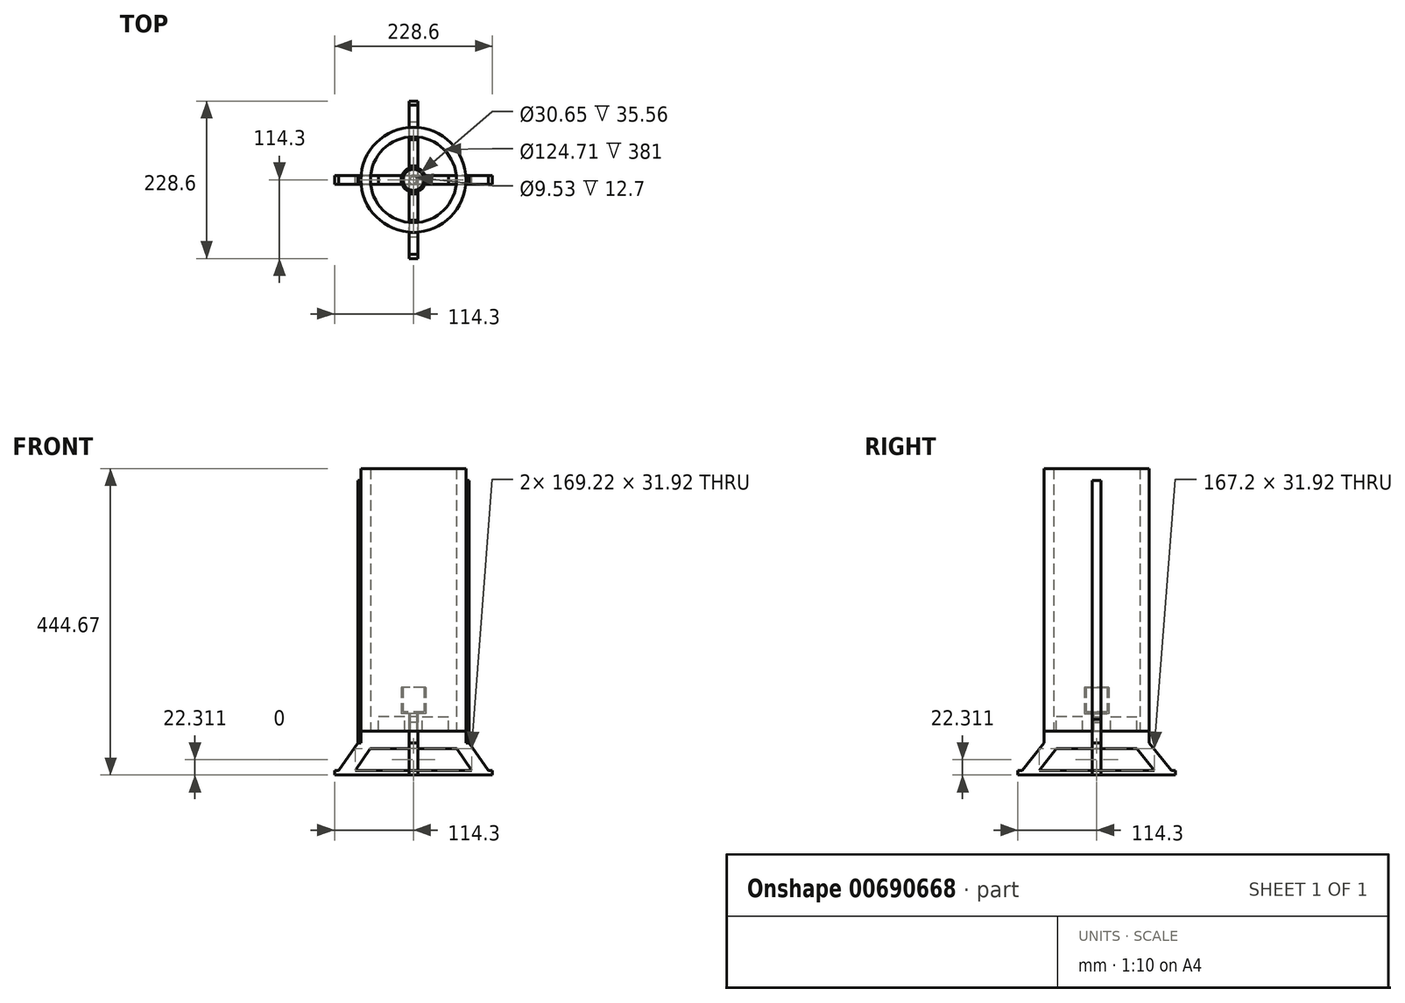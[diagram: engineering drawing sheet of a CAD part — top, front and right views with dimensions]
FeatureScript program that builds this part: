
annotation { "Feature Type Name" : "Feature", "Feature Type Description" : "" }
export const myFeature = defineFeature(function(context is Context, id is Id, definition is map)
    precondition{}
    {
        {
            var Q0;
            Q0=qCreatedBy(makeId("Top.planeOp"),FACE);
            var sketch = newSketch(context, id + "F0", { "sketchPlane" : qUnion([Q0])});
            skCircle(sketch, "E0", {"center": v(0, 0) * mm, "radius": 76.2 * mm});
            skCircle(sketch, "E1.0", {"center": v(0, 0) * mm, "radius": 62.36 * mm});
            skSolve(sketch);
        }
        {
            var Q0;
            Q0=qSketchRegion(id+"F0",true);
            extrude(context, id + "F1", {"entities" : qUnion([Q0]), "depth" : 381 * mm, "offsetDistance" : 25.4 * mm});
        }
        {
            var Q0;
            Q0=qCreatedBy(makeId("Front.planeOp"),FACE);
            var sketch = newSketch(context, id + "F2", { "sketchPlane" : qUnion([Q0])});
            skLineSegment(sketch, "E2", {"start": v(0, 0) * mm, "end": v(76.2, 0) * mm});
            skLineSegment(sketch, "E3", {"start": v(84.61, -57.32) * mm, "end": v(62.97, -25.4) * mm});
            skLineSegment(sketch, "E4", {"start": v(62.97, -25.4) * mm, "end": v(0, -25.4) * mm});
            skLineSegment(sketch, "E5", {"start": v(76.2, 0) * mm, "end": v(76.2, -16.95) * mm});
            skLineSegment(sketch, "E6", {"start": v(76.2, -16.95) * mm, "end": v(80.84, -16.95) * mm});
            skLineSegment(sketch, "E7", {"start": v(80.84, -16.95) * mm, "end": v(108.66, -57.32) * mm});
            skLineSegment(sketch, "E8", {"start": v(0, 0) * mm, "end": v(0, -25.4) * mm});
            skLineSegment(sketch, "E9", {"start": v(108.66, -57.32) * mm, "end": v(84.61, -57.32) * mm});
            skLineSegment(sketch, "E10.bottom", {"start": v(0, -57.32) * mm, "end": v(0, -57.32) * mm});
            skLineSegment(sketch, "E10.left", {"start": v(0, -57.32) * mm, "end": v(0, -63.67) * mm});
            skLineSegment(sketch, "E10.right", {"start": v(0, -57.32) * mm, "end": v(0, -63.67) * mm});
            skLineSegment(sketch, "E11.bottom", {"start": v(0, -57.32) * mm, "end": v(114.3, -57.32) * mm});
            skLineSegment(sketch, "E11.top", {"start": v(0, -63.67) * mm, "end": v(114.3, -63.67) * mm});
            skLineSegment(sketch, "E11.right", {"start": v(114.3, -57.32) * mm, "end": v(114.3, -63.67) * mm});
            skLineSegment(sketch, "E12.MirrorCS", {"start": v(-76.2, -16.95) * mm, "end": v(-80.84, -16.95) * mm});
            skLineSegment(sketch, "E13.MirrorCS", {"start": v(-76.2, 0) * mm, "end": v(-76.2, -16.95) * mm});
            skLineSegment(sketch, "E14.MirrorCS", {"start": v(-108.66, -57.32) * mm, "end": v(-84.61, -57.32) * mm});
            skLineSegment(sketch, "E15.MirrorCS", {"start": v(-114.3, -57.32) * mm, "end": v(-114.3, -63.67) * mm});
            skLineSegment(sketch, "E16.MirrorCS", {"start": v(-62.97, -25.4) * mm, "end": v(0, -25.4) * mm});
            skLineSegment(sketch, "E17.MirrorCS", {"start": v(0, -57.32) * mm, "end": v(-114.3, -57.32) * mm});
            skLineSegment(sketch, "E18.MirrorCS", {"start": v(0, -63.67) * mm, "end": v(-114.3, -63.67) * mm});
            skLineSegment(sketch, "E19.MirrorCS", {"start": v(-84.61, -57.32) * mm, "end": v(-62.97, -25.4) * mm});
            skLineSegment(sketch, "E20.MirrorCS", {"start": v(0, 0) * mm, "end": v(-76.2, 0) * mm});
            skLineSegment(sketch, "E21.MirrorCS", {"start": v(-80.84, -16.95) * mm, "end": v(-108.66, -57.32) * mm});
            skLineSegment(sketch, "E22.bottom", {"start": v(12.7, 0) * mm, "end": v(50.8, 0) * mm});
            skLineSegment(sketch, "E22.top", {"start": v(12.7, 21.11) * mm, "end": v(50.8, 21.11) * mm});
            skLineSegment(sketch, "E22.left", {"start": v(12.7, 0) * mm, "end": v(12.7, 21.11) * mm});
            skLineSegment(sketch, "E22.right", {"start": v(50.8, 0) * mm, "end": v(50.8, 21.11) * mm});
            skLineSegment(sketch, "E23.MirrorCS", {"start": v(-12.7, 0) * mm, "end": v(-12.7, 21.11) * mm});
            skLineSegment(sketch, "E24.MirrorCS", {"start": v(-12.7, 21.11) * mm, "end": v(-50.8, 21.11) * mm});
            skLineSegment(sketch, "E25.MirrorCS", {"start": v(-50.8, 0) * mm, "end": v(-50.8, 21.11) * mm});
            skSolve(sketch);
        }
        {
            var Q0;
            Q0=qSketchRegion(id+"F2",true);
            extrude(context, id + "F3", {"entities" : qUnion([Q0]), "endBound" : BoundingType.SYMMETRIC, "depth" : 12.7 * mm, "offsetDistance" : 25.4 * mm});
        }
        {
            var Q0;
            Q0=makeQuery(id+"F3.opExtrude","SWEPT_BODY",BODY,{"disambiguationData":[OSD([sQuery(id+"F2.wireOp",EDGE,"E2"),sQuery(id+"F2.wireOp",EDGE,"E3"),sQuery(id+"F2.wireOp",EDGE,"E4"),sQuery(id+"F2.wireOp",EDGE,"E5"),sQuery(id+"F2.wireOp",EDGE,"E6"),sQuery(id+"F2.wireOp",EDGE,"E7"),sQuery(id+"F2.wireOp",EDGE,"yYa1QQtk-rfeQ-uA0k-yN95-LENgFDuBBmhA"),sQuery(id+"F2.wireOp",EDGE,"RaL1Y38n-DL0R-HpUy-0Yu0-hKOuieMtGCDP"),sQuery(id+"F2.wireOp",EDGE,"KzeCX9vK-PA9l-fBDc-L8z4-hnWVkcK37siH"),sQuery(id+"F2.wireOp",EDGE,"7a3115bd-42c9-43fa-886f-b7d7f014f3800.MirrorCS"),sQuery(id+"F2.wireOp",EDGE,"93714e8b-1b55-43fa-9f0a-1818bfe9d4330.MirrorCS"),sQuery(id+"F2.wireOp",EDGE,"f685ec73-5cd7-40c9-a0cc-09a82770efb00.MirrorCS"),sQuery(id+"F2.wireOp",EDGE,"605de593-ab4b-4a38-8b95-8d2e6ad95e7e0.MirrorCS"),sQuery(id+"F2.wireOp",EDGE,"bd68596d-ea5b-43b6-8ec0-eaa4091035650.MirrorCS"),sQuery(id+"F2.wireOp",EDGE,"6dadb6d6-938b-41b2-89eb-21b29489f2620.MirrorCS"),sQuery(id+"F2.wireOp",EDGE,"35a6b2d6-89f1-42be-bee9-e52b24f0a85c0.MirrorCS"),sQuery(id+"F2.wireOp",EDGE,"99d46e2b-beb4-45a8-a67b-b38dd53197940.MirrorCS"),sQuery(id+"F2.wireOp",EDGE,"687b68df-4fec-4741-9a90-ace4315f9af80.MirrorCS")])]});
            transform(context, id + "F4", {"entities" : qUnion([Q0]), "transformType" : TransformType.COPY});
        }
        {
            var Q0;
            Q0=makeQuery(id+"F4.opPattern","COPY",FACE,{"derivedFrom":makeQuery(id+"F3.opExtrude","CAP_FACE",FACE,{"disambiguationData":[OSD([sQuery(id+"F2.wireOp",EDGE,"E2"),sQuery(id+"F2.wireOp",EDGE,"E3"),sQuery(id+"F2.wireOp",EDGE,"E4"),sQuery(id+"F2.wireOp",EDGE,"E5"),sQuery(id+"F2.wireOp",EDGE,"E6"),sQuery(id+"F2.wireOp",EDGE,"E7"),sQuery(id+"F2.wireOp",EDGE,"E11.bottom"),sQuery(id+"F2.wireOp",EDGE,"E11.top"),sQuery(id+"F2.wireOp",EDGE,"E11.right"),sQuery(id+"F2.wireOp",EDGE,"6d3937cc-c99b-4de3-b3db-85ad403e89ce3.MirrorCS"),sQuery(id+"F2.wireOp",EDGE,"E15.MirrorCS"),sQuery(id+"F2.wireOp",EDGE,"6d3937cc-c99b-4de3-b3db-85ad403e89ce8.MirrorCS"),sQuery(id+"F2.wireOp",EDGE,"E16.MirrorCS"),sQuery(id+"F2.wireOp",EDGE,"E17.MirrorCS"),sQuery(id+"F2.wireOp",EDGE,"E18.MirrorCS"),sQuery(id+"F2.wireOp",EDGE,"E19.MirrorCS"),sQuery(id+"F2.wireOp",EDGE,"E20.MirrorCS"),sQuery(id+"F2.wireOp",EDGE,"6d3937cc-c99b-4de3-b3db-85ad403e89ce15.MirrorCS"),sQuery(id+"F2.wireOp",EDGE,"E21.MirrorCS")])],"isStart":false}),"instanceName":"1"});
            var sketch = newSketch(context, id + "F5", { "sketchPlane" : qUnion([Q0])});
            skLineSegment(sketch, "E26.bottom", {"start": v(76.2, -16.95) * mm, "end": v(80.84, -16.95) * mm});
            skLineSegment(sketch, "E26.top", {"start": v(76.2, 364.05) * mm, "end": v(80.84, 364.05) * mm});
            skLineSegment(sketch, "E26.left", {"start": v(76.2, -16.95) * mm, "end": v(76.2, 364.05) * mm});
            skLineSegment(sketch, "E26.right", {"start": v(80.84, -16.95) * mm, "end": v(80.84, 364.05) * mm});
            skSolve(sketch);
        }
        {
            var Q0;
            {var subQ3=sQuery(id+"F5.wireOp",EDGE,"E26.bottom");Q0=makeQuery(id+"F5.imprint","IMPRINT",FACE,{"disambiguationData":[TD([[makeQuery(id+"F5.imprint","IMPRINT",EDGE,{"derivedFrom":subQ3}),1.0]])]});}
            extrude(context, id + "F6", {"entities" : qUnion([Q0]), "oppositeDirection" : true, "depth" : 12.7 * mm, "offsetDistance" : 25.4 * mm});
        }
        {
            var Q0;
            Q0=makeQuery(id+"F6.opExtrude","SWEPT_BODY",BODY,{"disambiguationData":[OSD([sQuery(id+"F5.wireOp",EDGE,"E26.bottom"),sQuery(id+"F5.wireOp",EDGE,"E26.top"),sQuery(id+"F5.wireOp",EDGE,"E26.left"),sQuery(id+"F5.wireOp",EDGE,"E26.right")])]});
            var Q1;
            Q1=sQuery(id+"F2.wireOp",EDGE,"E8");
            circularPattern(context, id + "F7", {"entities" : qUnion([Q0]), "axis" : qUnion([Q1]), "angle" : 360 * degree, "instanceCount" : 2, "equalSpace" : true});
        }
        {
            var Q0;
            Q0=makeQuery(id+"F3.opExtrude","CAP_FACE",FACE,{"disambiguationData":[OSD([sQuery(id+"F2.wireOp",EDGE,"E2"),sQuery(id+"F2.wireOp",EDGE,"E3"),sQuery(id+"F2.wireOp",EDGE,"E4"),sQuery(id+"F2.wireOp",EDGE,"E5"),sQuery(id+"F2.wireOp",EDGE,"E6"),sQuery(id+"F2.wireOp",EDGE,"E7"),sQuery(id+"F2.wireOp",EDGE,"E11.bottom"),sQuery(id+"F2.wireOp",EDGE,"E11.top"),sQuery(id+"F2.wireOp",EDGE,"E11.right"),sQuery(id+"F2.wireOp",EDGE,"E12.MirrorCS"),sQuery(id+"F2.wireOp",EDGE,"E13.MirrorCS"),sQuery(id+"F2.wireOp",EDGE,"E15.MirrorCS"),sQuery(id+"F2.wireOp",EDGE,"E16.MirrorCS"),sQuery(id+"F2.wireOp",EDGE,"E17.MirrorCS"),sQuery(id+"F2.wireOp",EDGE,"E18.MirrorCS"),sQuery(id+"F2.wireOp",EDGE,"E19.MirrorCS"),sQuery(id+"F2.wireOp",EDGE,"E20.MirrorCS"),sQuery(id+"F2.wireOp",EDGE,"E21.MirrorCS")])],"isStart":false});
            var sketch = newSketch(context, id + "F8", { "sketchPlane" : qUnion([Q0])});
            skLineSegment(sketch, "E27.bottom", {"start": v(76.2, -16.95) * mm, "end": v(80.84, -16.95) * mm});
            skLineSegment(sketch, "E27.top", {"start": v(76.2, 17.25) * mm, "end": v(80.84, 17.25) * mm});
            skLineSegment(sketch, "E27.left", {"start": v(76.2, -16.95) * mm, "end": v(76.2, 17.25) * mm});
            skLineSegment(sketch, "E27.right", {"start": v(80.84, -16.95) * mm, "end": v(80.84, 17.25) * mm});
            skSolve(sketch);
        }
        {
            var Q0;
            Q0=qSketchRegion(id+"F8",true);
            extrude(context, id + "F9", {"entities" : qUnion([Q0]), "oppositeDirection" : true, "depth" : 12.7 * mm, "offsetDistance" : 25.4 * mm});
        }
        {
            var Q0;
            Q0=makeQuery(id+"F9.opExtrude","SWEPT_BODY",BODY,{"disambiguationData":[OSD([sQuery(id+"F8.wireOp",EDGE,"E27.bottom"),sQuery(id+"F8.wireOp",EDGE,"E27.top"),sQuery(id+"F8.wireOp",EDGE,"E27.left"),sQuery(id+"F8.wireOp",EDGE,"E27.right")])]});
            var Q1;
            Q1=sQuery(id+"F2.wireOp",EDGE,"E8");
            circularPattern(context, id + "F10", {"entities" : qUnion([Q0]), "axis" : qUnion([Q1]), "angle" : 360 * degree, "instanceCount" : 2, "equalSpace" : true});
        }
        {
            var Q0;
            Q0=qCreatedBy(makeId("Right.planeOp"),FACE);
            cPlane(context, id + "F11", {"entities" : qUnion([Q0]), "cplaneType" : CPlaneType.OFFSET, "offset" : 0 * mm, "oppositeDirection" : true, "width" : 152.4 * mm, "height" : 152.4 * mm});
        }
        {
            var Q0;
            Q0=qCreatedBy(id+"F11.planeOp",FACE);
            var sketch = newSketch(context, id + "F12", { "sketchPlane" : qUnion([Q0])});
            skLineSegment(sketch, "E28.bottom", {"start": v(-109.95, 11.2) * mm, "end": v(-109.95, 11.2) * mm});
            skLineSegment(sketch, "E29.0", {"start": v(0, 0) * mm, "end": v(0, -25.4) * mm});
            skLineSegment(sketch, "E30", {"start": v(0, 0) * mm, "end": v(76.2, 0) * mm});
            skLineSegment(sketch, "E31", {"start": v(83.6, -57.32) * mm, "end": v(58.33, -25.4) * mm});
            skLineSegment(sketch, "E32", {"start": v(58.33, -25.4) * mm, "end": v(0, -25.4) * mm});
            skLineSegment(sketch, "E33", {"start": v(76.2, 0) * mm, "end": v(76.2, -16.95) * mm});
            skLineSegment(sketch, "E34", {"start": v(71.56, -16.95) * mm, "end": v(76.2, -16.95) * mm});
            skLineSegment(sketch, "E35", {"start": v(76.2, -16.95) * mm, "end": v(108.16, -57.32) * mm});
            skLineSegment(sketch, "E36", {"start": v(108.16, -57.32) * mm, "end": v(83.6, -57.32) * mm});
            skLineSegment(sketch, "E37.bottom", {"start": v(5.11, -2.13) * mm, "end": v(5.11, -2.13) * mm});
            skLineSegment(sketch, "E38.bottom", {"start": v(-1.08, -57.32) * mm, "end": v(114.3, -57.32) * mm});
            skLineSegment(sketch, "E38.top", {"start": v(-1.08, -63.67) * mm, "end": v(114.3, -63.67) * mm});
            skLineSegment(sketch, "E38.right", {"start": v(114.3, -57.32) * mm, "end": v(114.3, -63.67) * mm});
            skLineSegment(sketch, "E39.MirrorCS", {"start": v(-76.2, 0) * mm, "end": v(-76.2, -16.95) * mm});
            skLineSegment(sketch, "E40.MirrorCS", {"start": v(-108.16, -57.32) * mm, "end": v(-83.6, -57.32) * mm});
            skLineSegment(sketch, "E41.MirrorCS", {"start": v(-114.3, -57.32) * mm, "end": v(-114.3, -63.67) * mm});
            skLineSegment(sketch, "E42.MirrorCS", {"start": v(-58.33, -25.4) * mm, "end": v(0, -25.4) * mm});
            skLineSegment(sketch, "E43.MirrorCS", {"start": v(1.08, -57.32) * mm, "end": v(-114.3, -57.32) * mm});
            skLineSegment(sketch, "E44.MirrorCS", {"start": v(1.08, -63.67) * mm, "end": v(-114.3, -63.67) * mm});
            skLineSegment(sketch, "E45.MirrorCS", {"start": v(-83.6, -57.32) * mm, "end": v(-58.33, -25.4) * mm});
            skLineSegment(sketch, "E46.MirrorCS", {"start": v(0, 0) * mm, "end": v(-76.2, 0) * mm});
            skLineSegment(sketch, "E47.MirrorCS", {"start": v(-76.2, -16.95) * mm, "end": v(-108.16, -57.32) * mm});
            skLineSegment(sketch, "E48.bottom", {"start": v(-20.32, 0) * mm, "end": v(-58.42, 0) * mm});
            skLineSegment(sketch, "E48.top", {"start": v(-20.32, 21.11) * mm, "end": v(-58.42, 21.11) * mm});
            skLineSegment(sketch, "E48.left", {"start": v(-20.32, 0) * mm, "end": v(-20.32, 21.11) * mm});
            skLineSegment(sketch, "E48.right", {"start": v(-58.42, 0) * mm, "end": v(-58.42, 21.11) * mm});
            skPoint(sketch, "E49.0", {"position": v(0, 21.11) * mm});
            skLineSegment(sketch, "E50", {"start": v(0, 21.11) * mm, "end": v(-20.32, 21.11) * mm, "construction": true});
            skLineSegment(sketch, "E51.MirrorCS", {"start": v(20.32, 0) * mm, "end": v(20.32, 21.11) * mm});
            skLineSegment(sketch, "E52.MirrorCS", {"start": v(20.32, 21.11) * mm, "end": v(58.42, 21.11) * mm});
            skLineSegment(sketch, "E53.MirrorCS", {"start": v(58.42, 0) * mm, "end": v(58.42, 21.11) * mm});
            skSolve(sketch);
        }
        {
            var Q0;
            Q0 = qSketchRegion(id + "F12", true);
            extrude(context, id + "F13", {"entities" : qUnion([Q0]), "endBound" : BoundingType.SYMMETRIC, "depth" : 12.7 * mm, "offsetDistance" : 25.4 * mm});
        }
        {
            var Q0;
            Q0=qCreatedBy(makeId("Top.planeOp"),FACE);
            var sketch = newSketch(context, id + "F14", { "sketchPlane" : qUnion([Q0])});
            skPoint(sketch, "E54.0", {"position": v(0, 0) * mm});
            skCircle(sketch, "E55", {"center": v(0, 0) * mm, "radius": 4.76 * mm});
            skSolve(sketch);
        }
        {
            var Q0;
            Q0 = qSketchRegion(id + "F14", true);
            extrude(context, id + "F15", {"entities" : qUnion([Q0]), "depth" : 12.7 * mm, "offsetDistance" : 25.4 * mm});
        }
        {
            var Q0;
            Q0=makeQuery(id+"F15.opExtrude","CAP_FACE",FACE,{"disambiguationData":[OSD([sQuery(id+"F14.wireOp",EDGE,"E55")])],"isStart":false});
            var sketch = newSketch(context, id + "F16", { "sketchPlane" : qUnion([Q0])});
            skCircle(sketch, "E56.0.0", {"center": v(0, 0) * mm, "radius": 4.76 * mm});
            skCircle(sketch, "E57", {"center": v(0, 0) * mm, "radius": 6.61 * mm});
            skSolve(sketch);
        }
        {
            var Q0;
            Q0 = qSketchRegion(id + "F16", true);
            extrude(context, id + "F17", {"entities" : qUnion([Q0]), "depth" : 12.7 * mm, "offsetDistance" : 25.4 * mm});
        }
        {
            var Q0;
            Q0=makeQuery(id+"F17.opExtrude","CAP_FACE",FACE,{"disambiguationData":[OSD([sQuery(id+"F16.wireOp",EDGE,"E56.0.0"),sQuery(id+"F16.wireOp",EDGE,"E57")])],"isStart":false});
            var sketch = newSketch(context, id + "F18", { "sketchPlane" : qUnion([Q0])});
            skCircle(sketch, "E58", {"center": v(0, 0) * mm, "radius": 17.86 * mm});
            skSolve(sketch);
        }
        {
            var Q0;
            Q0 = qSketchRegion(id + "F18", true);
            extrude(context, id + "F19", {"entities" : qUnion([Q0]), "depth" : 38.1 * mm, "offsetDistance" : 25.4 * mm});
        }
        {
            var Q0;
            Q0=makeQuery(id+"F19.opExtrude","CAP_FACE",FACE,{"disambiguationData":[OSD([sQuery(id+"F18.wireOp",EDGE,"E58")])],"isStart":false});
            shell(context, id + "F20", {"entities" : qUnion([Q0]), "thickness" : 2.54 * mm});
        }
    });
